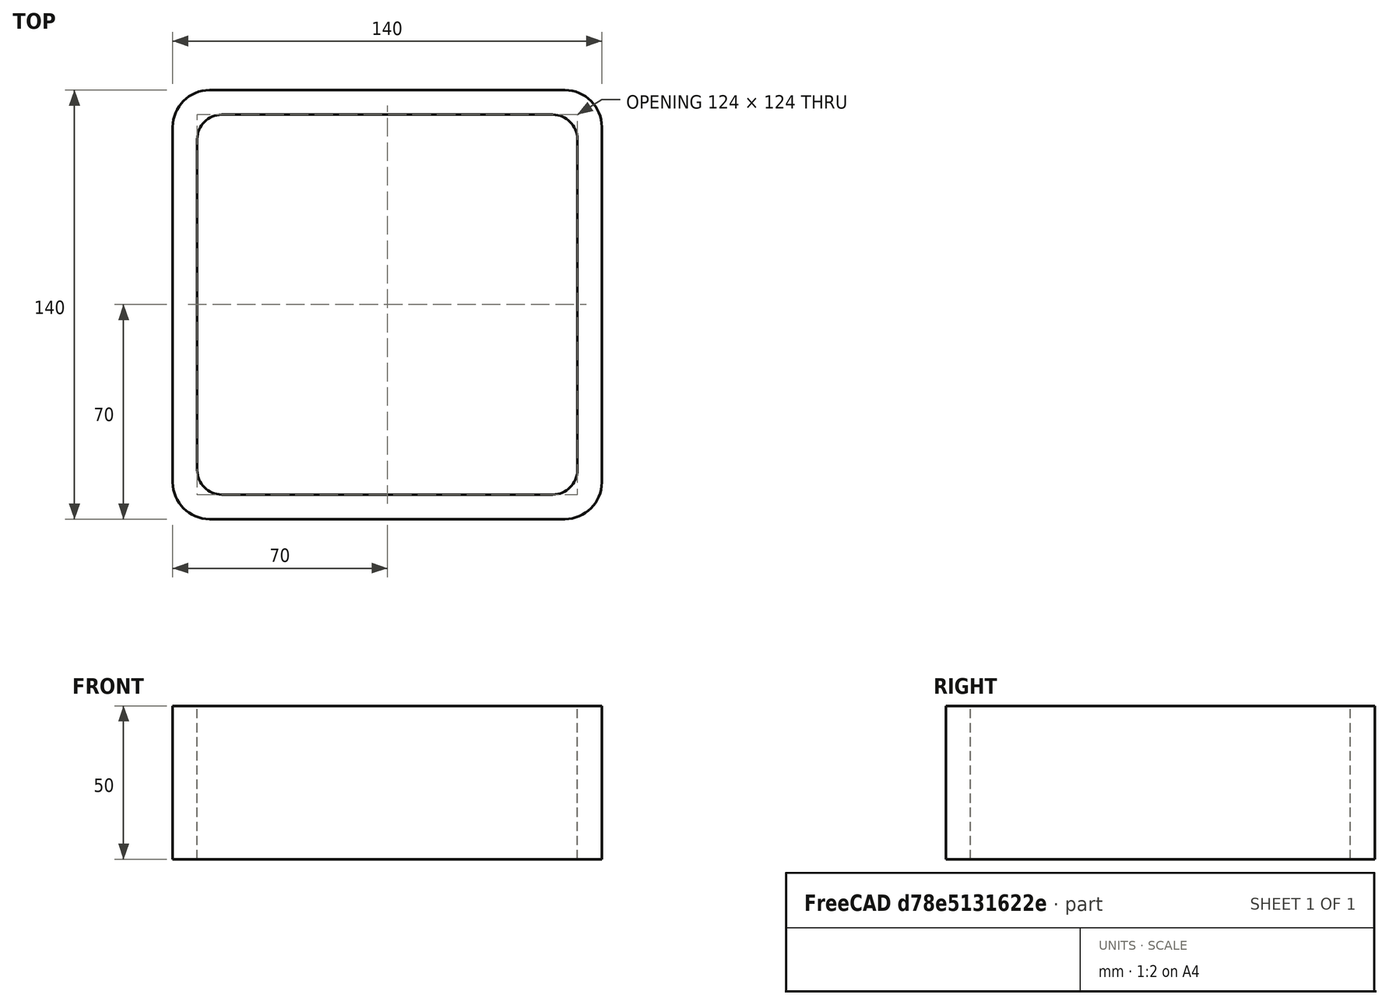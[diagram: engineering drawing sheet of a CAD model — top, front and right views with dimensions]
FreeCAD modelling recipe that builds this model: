
FCSTD DOCUMENT  (FreeCAD 0.15R4671 (Git))
Label: Square hollow section 140x140x8 EN10219 S235JRH
License: All rights reserved
LicenseURL: http://en.wikipedia.org/wiki/All_rights_reserved
objects: Sketcher::SketchObject×1, Part::Extrusion×1
note: 2 computed .brp shape members not serialized (recipe doc carries the construction recipe); baked Part::Feature solids carry a one-line shape summary decoded from their .brp

FEATURE [Sketcher::SketchObject] Sketch
  sketch-geometry (16):
    g0: LineSegment StartX=-54 StartY=62 StartZ=0 EndX=54 EndY=62 EndZ=0
    g1: LineSegment StartX=62 StartY=54 StartZ=0 EndX=62 EndY=-54 EndZ=0
    g2: LineSegment StartX=54 StartY=-62 StartZ=0 EndX=-54 EndY=-62 EndZ=0
    g3: LineSegment StartX=-62 StartY=-54 StartZ=0 EndX=-62 EndY=54 EndZ=0
    g4: LineSegment StartX=-58 StartY=70 StartZ=0 EndX=58 EndY=70 EndZ=0
    g5: LineSegment StartX=70 StartY=58 StartZ=0 EndX=70 EndY=-58 EndZ=0
    g6: LineSegment StartX=58 StartY=-70 StartZ=0 EndX=-58 EndY=-70 EndZ=0
    g7: LineSegment StartX=-70 StartY=-58 StartZ=0 EndX=-70 EndY=58 EndZ=0
    g8: ArcOfCircle CenterX=-54 CenterY=54 CenterZ=0 NormalX=0 NormalY=0 NormalZ=1 Radius=8 StartAngle=1.5708 EndAngle=3.14159
    g9: ArcOfCircle CenterX=54 CenterY=54 CenterZ=0 NormalX=0 NormalY=0 NormalZ=1 Radius=8 StartAngle=0 EndAngle=1.5708
    g10: ArcOfCircle CenterX=54 CenterY=-54 CenterZ=0 NormalX=0 NormalY=0 NormalZ=1 Radius=8 StartAngle=4.71239 EndAngle=6.28319
    g11: ArcOfCircle CenterX=-54 CenterY=-54 CenterZ=0 NormalX=0 NormalY=0 NormalZ=1 Radius=8 StartAngle=3.14159 EndAngle=4.71239
    g12: ArcOfCircle CenterX=58 CenterY=58 CenterZ=0 NormalX=0 NormalY=0 NormalZ=1 Radius=12 StartAngle=0 EndAngle=1.5708
    g13: ArcOfCircle CenterX=58 CenterY=-58 CenterZ=0 NormalX=0 NormalY=0 NormalZ=1 Radius=12 StartAngle=4.71239 EndAngle=6.28319
    g14: ArcOfCircle CenterX=-58 CenterY=-58 CenterZ=0 NormalX=0 NormalY=0 NormalZ=1 Radius=12 StartAngle=3.14159 EndAngle=4.71239
    g15: ArcOfCircle CenterX=-58 CenterY=58 CenterZ=0 NormalX=0 NormalY=0 NormalZ=1 Radius=12 StartAngle=1.5708 EndAngle=3.14159
  constraints (36):
    c: Horizontal(g2)
    c: Vertical(g3)
    c: Horizontal(g6)
    c: Vertical(g7)
    c: Tangent(g3,g8) = 1.5708
    c: Tangent(g0,g8) = 1.5708
    c: Tangent(g0,g9) = 1.5708
    c: Tangent(g1,g9) = 1.5708
    c: Tangent(g1,g10) = 1.5708
    c: Tangent(g2,g10) = 1.5708
    c: Tangent(g2,g11) = 1.5708
    c: Tangent(g3,g11) = 1.5708
    c: Tangent(g4,g12) = 1.5708
    c: Tangent(g5,g12) = 1.5708
    c: Tangent(g5,g13) = 1.5708
    c: Tangent(g6,g13) = 1.5708
    c: Tangent(g6,g14) = 1.5708
    c: Tangent(g7,g14) = 1.5708
    c: Tangent(g7,g15) = 1.5708
    c: Tangent(g4,g15) = 1.5708
    c: Equal(g9,g8)
    c: Equal(g9,g11)
    c: Equal(g9,g10)
    c: Equal(g12,g15)
    c: Equal(g12,g14)
    c: Equal(g12,g13)
    c: Symmetric(g4,g6,g-1)
    c: Symmetric(g7,g5,g-2)
    c: DistanceY(g4,g6) = -140
    c: DistanceX(g7,g5) = 140
    c: Symmetric(g3,g1,g-2)
    c: Symmetric(g0,g2,g-1)
    c: DistanceY(g0,g4) = 8
    c: DistanceX(g5,g1) = -8
    c: Radius(g9) = 8
    c: Radius(g12) = 12
FEATURE [Part::Extrusion] Extrude  label="Square hollow section 140x140x8 EN10219 S235JRH"
  Base = -> Sketch
  Dir = (0,0,50)
  Solid = true
